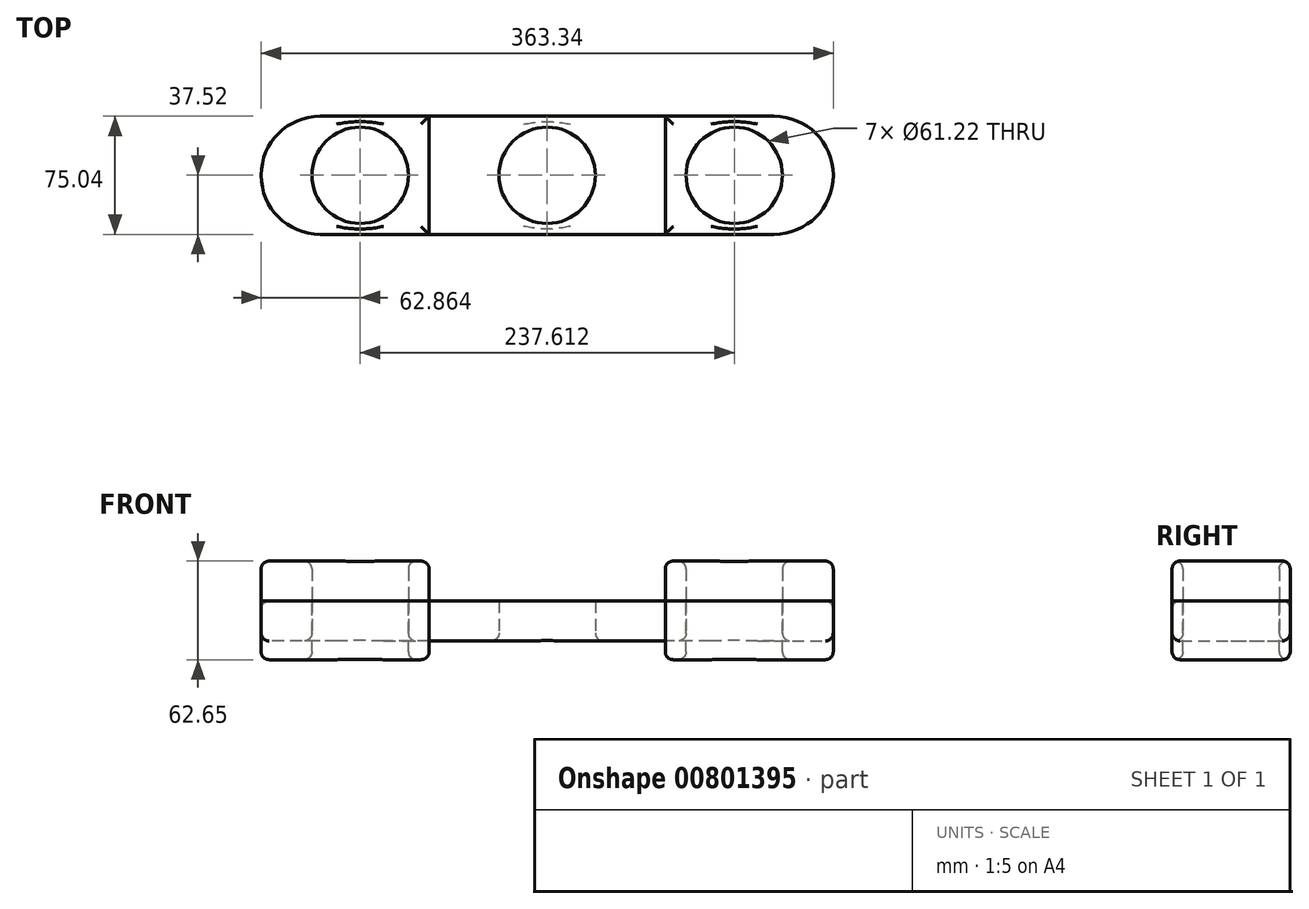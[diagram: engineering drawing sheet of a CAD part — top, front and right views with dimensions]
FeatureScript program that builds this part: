
annotation { "Feature Type Name" : "Feature", "Feature Type Description" : "" }
export const myFeature = defineFeature(function(context is Context, id is Id, definition is map)
    precondition{}
    {
        {
            var Q0;
            Q0=qCreatedBy(makeId("Top.planeOp"),FACE);
            var sketch = newSketch(context, id + "F0", { "sketchPlane" : qUnion([Q0])});
            skLineSegment(sketch, "E0.bottom", {"start": v(144.15, -37.52) * mm, "end": v(-144.15, -37.52) * mm});
            skLineSegment(sketch, "E0.top", {"start": v(144.15, 37.52) * mm, "end": v(-144.15, 37.52) * mm});
            skPoint(sketch, "E0.middle", {"position": v(0, 0) * mm});
            skCircle(sketch, "E1", {"center": v(0, 0) * mm, "radius": 30.61 * mm});
            skArc(sketch, "E2", {"start": v(144.15, 37.52) * mm, "mid": v(181.67, 0) * mm, "end": v(144.15, -37.52) * mm});
            skLineSegment(sketch, "E3", {"start": v(59.4, 37.52) * mm, "end": v(59.4, -37.52) * mm});
            skCircle(sketch, "E4.MirrorC", {"center": v(118.8, 0) * mm, "radius": 30.61 * mm});
            skLineSegment(sketch, "E5", {"start": v(0, 37.52) * mm, "end": v(0, -37.52) * mm});
            skCircle(sketch, "E6.MirrorC", {"center": v(-118.8, 0) * mm, "radius": 30.61 * mm});
            skArc(sketch, "E7.MirrorCS", {"start": v(-144.15, 37.52) * mm, "mid": v(-181.67, 0) * mm, "end": v(-144.15, -37.52) * mm});
            skSolve(sketch);
        }
        {
            var Q0;
            Q0 = qSketchRegion(id + "F0", true);
            extrude(context, id + "F1", {"entities" : qUnion([Q0]), "depth" : 25.4 * mm, "offsetDistance" : 25.4 * mm});
        }
        {
            var Q0;
            Q0=makeQuery(id+"F1.opExtrude","CAP_FACE",FACE,{"disambiguationData":[OSD([sQuery(id+"F0.wireOp",EDGE,"E0.bottom"),sQuery(id+"F0.wireOp",EDGE,"E0.top"),sQuery(id+"F0.wireOp",EDGE,"E1"),sQuery(id+"F0.wireOp",EDGE,"E2"),sQuery(id+"F0.wireOp",EDGE,"E4.MirrorC"),sQuery(id+"F0.wireOp",EDGE,"E6.MirrorC"),sQuery(id+"F0.wireOp",EDGE,"E7.MirrorCS")])],"isStart":false});
            var sketch = newSketch(context, id + "F2", { "sketchPlane" : qUnion([Q0])});
            skLineSegment(sketch, "E8", {"start": v(-75, 37.52) * mm, "end": v(-75, -37.52) * mm});
            skLineSegment(sketch, "E9", {"start": v(0, 37.52) * mm, "end": v(0, -37.52) * mm});
            skLineSegment(sketch, "E10.MirrorCS", {"start": v(75, 37.52) * mm, "end": v(75, -37.52) * mm});
            skSolve(sketch);
        }
        {
            var Q0;
            Q0=makeQuery(id+"F1.opExtrude","CAP_EDGE",EDGE,{"disambiguationData":[OSD([sQuery(id+"F0.wireOp",EDGE,"E0.top")])],"isStart":false});
            fillet(context, id + "F3", {"entities" : qUnion([Q0]), "radius" : 5.08 * mm, "tangentPropagation" : true, "allowEdgeOverflow" : false});
        }
        {
            var Q0;
            Q0=makeQuery(id+"F1.opExtrude","CAP_FACE",FACE,{"disambiguationData":[OSD([sQuery(id+"F0.wireOp",EDGE,"E0.bottom"),sQuery(id+"F0.wireOp",EDGE,"E0.top"),sQuery(id+"F0.wireOp",EDGE,"E1"),sQuery(id+"F0.wireOp",EDGE,"E2"),sQuery(id+"F0.wireOp",EDGE,"E4.MirrorC"),sQuery(id+"F0.wireOp",EDGE,"E6.MirrorC"),sQuery(id+"F0.wireOp",EDGE,"E7.MirrorCS")])],"isStart":true});
            var Q1;
            Q1=makeQuery(id+"F1.opExtrude","CAP_EDGE",EDGE,{"disambiguationData":[OSD([sQuery(id+"F0.wireOp",EDGE,"E0.top")])],"isStart":true});
            fillet(context, id + "F4", {"entities" : qUnion([Q0, Q1]), "radius" : 5.08 * mm, "tangentPropagation" : true, "allowEdgeOverflow" : false});
        }
        {
            var Q0;
            {var subQ2=sQuery(id+"F2.wireOp",EDGE,"E8");Q0=makeQuery(id+"F2.imprint","IMPRINT",FACE,{"disambiguationData":[TD([[makeQuery(id+"F2.imprint","IMPRINT",EDGE,{"derivedFrom":subQ2}),-1.0]])]});}
            var Q1;
            {var subQ2=sQuery(id+"F2.wireOp",EDGE,"E10.MirrorCS");Q1=makeQuery(id+"F2.imprint","IMPRINT",FACE,{"disambiguationData":[TD([[makeQuery(id+"F2.imprint","IMPRINT",EDGE,{"derivedFrom":subQ2}),1.0]])]});}
            extrude(context, id + "F5", {"entities" : qUnion([Q0, Q1]), "oppositeDirection" : true, "depth" : 37.25 * mm, "offsetDistance" : 25.4 * mm});
        }
        {
            var Q0;
            Q0=makeQuery(id+"F5.opExtrude","CAP_FACE",FACE,{"disambiguationData":[OSD([sQuery(id+"F0.wireOp",EDGE,"E0.bottom"),sQuery(id+"F0.wireOp",EDGE,"E0.top"),sQuery(id+"F0.wireOp",EDGE,"E6.MirrorC"),sQuery(id+"F0.wireOp",EDGE,"E7.MirrorCS"),sQuery(id+"F2.wireOp",EDGE,"E8")])],"isStart":true});
            extrude(context, id + "F6", {"entities" : qUnion([Q0]), "depth" : 25.4 * mm, "offsetDistance" : 25.4 * mm});
        }
        {
            var Q0;
            Q0=makeQuery(id+"F5.opExtrude","CAP_FACE",FACE,{"disambiguationData":[OSD([sQuery(id+"F0.wireOp",EDGE,"E0.bottom"),sQuery(id+"F0.wireOp",EDGE,"E0.top"),sQuery(id+"F0.wireOp",EDGE,"E2"),sQuery(id+"F0.wireOp",EDGE,"E4.MirrorC"),sQuery(id+"F2.wireOp",EDGE,"E10.MirrorCS")])],"isStart":true});
            extrude(context, id + "F7", {"entities" : qUnion([Q0]), "depth" : 25.4 * mm, "offsetDistance" : 25.4 * mm});
        }
        {
            var Q0;
            Q0=makeQuery(id+"F5.opExtrude","CAP_EDGE",EDGE,{"disambiguationData":[OSD([sQuery(id+"F0.wireOp",EDGE,"E2")])],"isStart":false});
            var Q1;
            Q1=makeQuery(id+"F5.opExtrude","CAP_EDGE",EDGE,{"disambiguationData":[OSD([sQuery(id+"F0.wireOp",EDGE,"E4.MirrorC")])],"isStart":false});
            var Q2;
            Q2=makeQuery(id+"F5.opExtrude","CAP_FACE",FACE,{"disambiguationData":[OSD([sQuery(id+"F0.wireOp",EDGE,"E0.bottom"),sQuery(id+"F0.wireOp",EDGE,"E0.top"),sQuery(id+"F0.wireOp",EDGE,"E2"),sQuery(id+"F0.wireOp",EDGE,"E4.MirrorC"),sQuery(id+"F2.wireOp",EDGE,"E10.MirrorCS")])],"isStart":false});
            fillet(context, id + "F8", {"entities" : qUnion([Q0, Q1, Q2]), "radius" : 5.08 * mm, "tangentPropagation" : true, "allowEdgeOverflow" : false});
        }
        {
            var Q0;
            Q0=makeQuery(id+"F7.opExtrude","CAP_EDGE",EDGE,{"disambiguationData":[OSD([sQuery(id+"F0.wireOp",EDGE,"E0.bottom")])],"isStart":false});
            var Q1;
            Q1=makeQuery(id+"F7.opExtrude","CAP_EDGE",EDGE,{"disambiguationData":[OSD([sQuery(id+"F0.wireOp",EDGE,"E4.MirrorC")])],"isStart":false});
            var Q2;
            Q2=makeQuery(id+"F7.opExtrude","CAP_EDGE",EDGE,{"disambiguationData":[OSD([sQuery(id+"F2.wireOp",EDGE,"E10.MirrorCS")])],"isStart":false});
            fillet(context, id + "F9", {"entities" : qUnion([Q0, Q1, Q2]), "radius" : 5.08 * mm, "tangentPropagation" : true, "allowEdgeOverflow" : false});
        }
        {
            var Q0;
            Q0=makeQuery(id+"F6.opExtrude","CAP_EDGE",EDGE,{"disambiguationData":[OSD([sQuery(id+"F0.wireOp",EDGE,"E6.MirrorC")])],"isStart":false});
            var Q1;
            Q1=makeQuery(id+"F6.opExtrude","CAP_EDGE",EDGE,{"disambiguationData":[OSD([sQuery(id+"F0.wireOp",EDGE,"E7.MirrorCS")])],"isStart":false});
            var Q2;
            Q2=makeQuery(id+"F6.opExtrude","CAP_EDGE",EDGE,{"disambiguationData":[OSD([sQuery(id+"F2.wireOp",EDGE,"E8")])],"isStart":false});
            fillet(context, id + "F10", {"entities" : qUnion([Q0, Q1, Q2]), "radius" : 5.08 * mm, "tangentPropagation" : true, "allowEdgeOverflow" : false});
        }
        {
            var Q0;
            {var subQ0=sQuery(id+"F0.wireOp",EDGE,"E0.bottom");var subQ1=makeQuery(id+"F1.opExtrude","CAP_EDGE",EDGE,{"disambiguationData":[OSD([subQ0])],"isStart":false});Q0=makeQuery(id+"F5.opExtrude","CAP_EDGE",EDGE,{"disambiguationData":[OSD([subQ0]),TDD([makeQuery(id+"F2.imprint","IMPRINT",EDGE,{"disambiguationData":[TD([[makeQuery(id+"F2.imprint","INTERSECT",VERTEX,{"derivedFrom":[subQ1,makeQuery(id+"F1.opExtrude","CAP_EDGE",EDGE,{"disambiguationData":[OSD([sQuery(id+"F0.wireOp",EDGE,"E7.MirrorCS")])],"isStart":false})]}),1.0]])],"derivedFrom":subQ1})])],"isStart":false});}
            var Q1;
            Q1=makeQuery(id+"F5.opExtrude","CAP_EDGE",EDGE,{"disambiguationData":[OSD([sQuery(id+"F0.wireOp",EDGE,"E6.MirrorC")])],"isStart":false});
            var Q2;
            Q2=makeQuery(id+"F5.opExtrude","CAP_EDGE",EDGE,{"disambiguationData":[OSD([sQuery(id+"F2.wireOp",EDGE,"E8")])],"isStart":false});
            fillet(context, id + "F11", {"entities" : qUnion([Q0, Q1, Q2]), "radius" : 5.08 * mm, "tangentPropagation" : true, "allowEdgeOverflow" : false});
        }
    });
